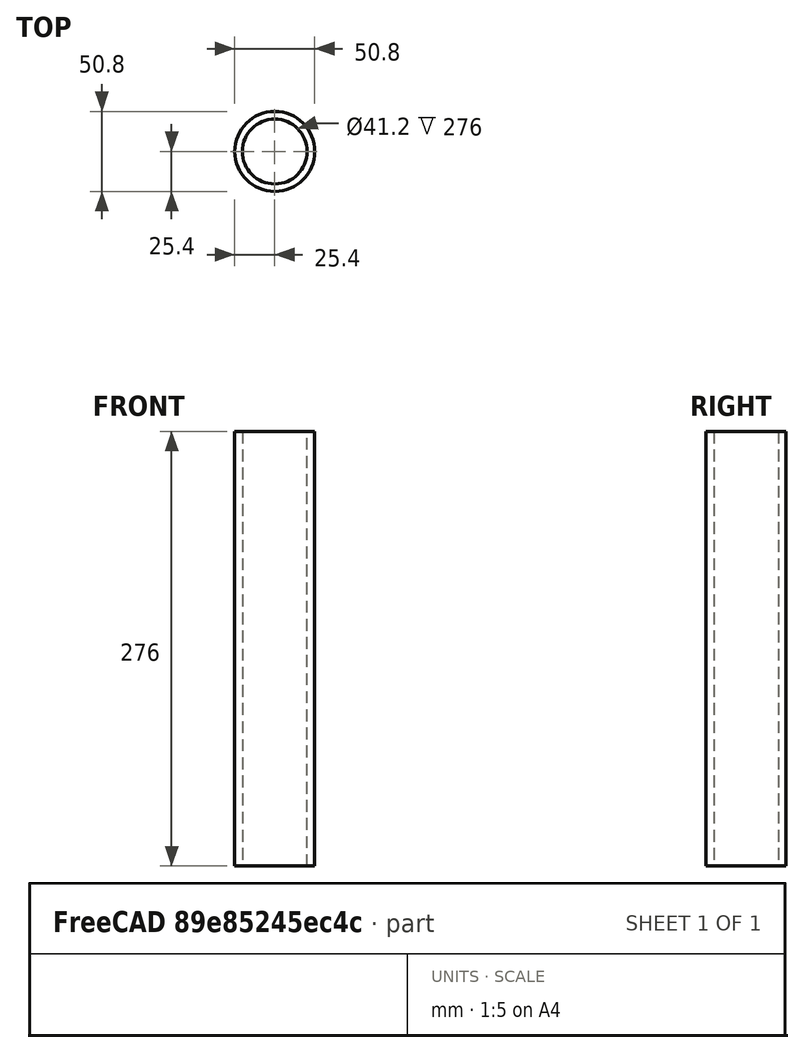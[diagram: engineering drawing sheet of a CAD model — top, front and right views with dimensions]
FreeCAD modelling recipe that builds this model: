
FCSTD DOCUMENT  (FreeCAD 0.19R24267 +99 (Git))
Label: Steel tube spacer 276mm length
License: All rights reserved
LicenseURL: http://en.wikipedia.org/wiki/All_rights_reserved
objects: Sketcher::SketchObject×1, PartDesign::Pad×1, PartDesign::Body×1
note: 4 computed .brp shape members not serialized (recipe doc carries the construction recipe); baked Part::Feature solids carry a one-line shape summary decoded from their .brp

FEATURE [Sketcher::SketchObject] Sketch  label="Cross section"
  FullyConstrained = true
  MapMode = 5
  Support = -> [XY_Plane]
  sketch-geometry (4):
    g0: Circle CenterX=0 CenterY=0 CenterZ=0 NormalX=0 NormalY=0 NormalZ=1 AngleXU=0 Radius=20.6
    g1: Circle CenterX=0 CenterY=0 CenterZ=0 NormalX=0 NormalY=0 NormalZ=1 AngleXU=0 Radius=25.4
    g2: GeomPoint X=20.6 Y=0 Z=0
    g3: GeomPoint X=25.4 Y=0 Z=0
  constraints (8):
    c: Coincident(g0,g-1)
    c: Coincident(g1,g0)
    c: PointOnObject(g2,g0)
    c: PointOnObject(g3,g1)
    c: PointOnObject(g3,g-1)
    c: PointOnObject(g2,g-1)
    c: DistanceX(g2,g3) = 4.8
    c: Diameter(g1) = 50.8
FEATURE [PartDesign::Pad] Pad  label="Length"
  Direction = (1,1,1)
  Length = 276
  Length2 = 100
  Profile = -> Sketch
  Type = 0
FEATURE [PartDesign::Body] Body
  Group = -> [Sketch,Pad]
  Origin = -> Origin
  Tip = -> Pad
